# Revit family: Sink-Pedestal-KOHLER-Folio-K-11340IN_1
name_source: partatom
category: Specialty Equipment
revit_build: Autodesk Revit 2017 (Build: 20160225_1515(x64)
units: mm (PartAtom-declared; Revit-internal decimal feet)

## family parameters
Cut with Voids When Loaded = No
Host = Face
OmniClass Number = 23.31.25.00
OmniClass Title = Toilet and Bath Specialties
Part Type = Normal
Room Calculation Point = No
Round Connector Dimension = Use Diameter
Shared = No

## types (2) — shared parameters
ADA Compliant = No
Assembly Code = C1030200
Date Modified = 06/25/2020
Default Elevation = 25"
Description = Half Pedestal
Height = 10 3/16"
Length = 11 7/16"
Manufacturer = KOHLER Co.
Master Format 2014 = 10 28 16
Master Format 2014 Name = Bath Accessories
Material = Vitreous China
Product Name = Folio
URL = https://www.kohler.co.in
WaterSense Certified = No
Width = 9 1/4"

## per-type parameters (varying)
| type | Finish | Model | Type |
| 0-White | Kohler-Vitreous_China-0-White | K-11340IN-0 | 1 |
| 96-Biscuit | Kohler-Vitreous_China-96-Biscuit | K-11340IN-96 | 2 |

## geometry (parser evidence)
native form markers: Sweep x4
no freeform markers — native parametric forms only
